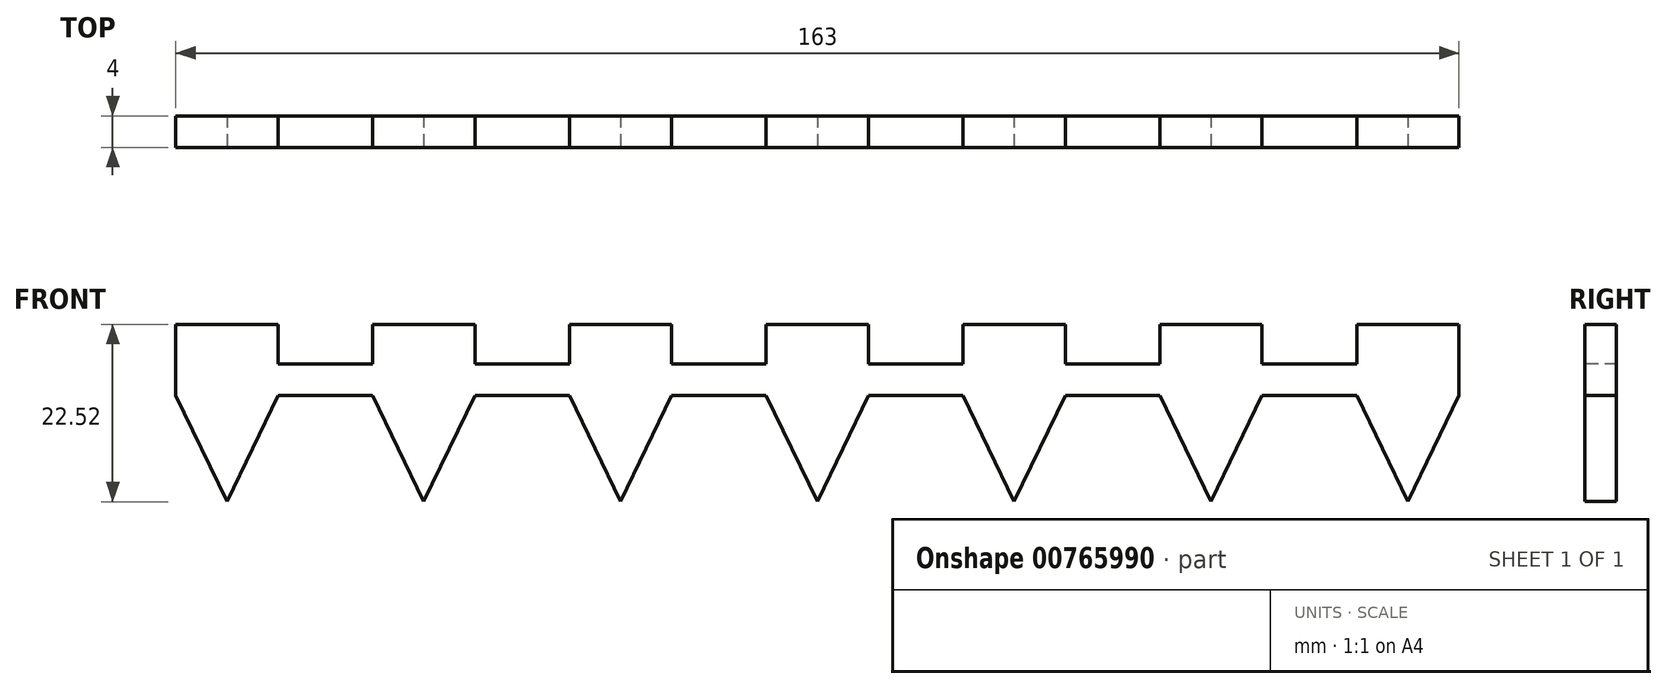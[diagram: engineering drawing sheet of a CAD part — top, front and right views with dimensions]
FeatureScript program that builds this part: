
annotation { "Feature Type Name" : "Feature", "Feature Type Description" : "" }
export const myFeature = defineFeature(function(context is Context, id is Id, definition is map)
    precondition{}
    {
        {
            var Q0;
            Q0=qCreatedBy(makeId("Top.planeOp"),FACE);
            var sketch = newSketch(context, id + "F0", { "sketchPlane" : qUnion([Q0])});
            skLineSegment(sketch, "E0.bottom", {"start": v(0, 0) * mm, "end": v(13, 0) * mm});
            skLineSegment(sketch, "E0.top", {"start": v(0, 4) * mm, "end": v(13, 4) * mm});
            skLineSegment(sketch, "E0.left", {"start": v(0, 0) * mm, "end": v(0, 4) * mm});
            skLineSegment(sketch, "E0.right", {"start": v(13, 0) * mm, "end": v(13, 4) * mm});
            skLineSegment(sketch, "E1.1.0.0", {"start": v(25, 4) * mm, "end": v(38, 4) * mm});
            skLineSegment(sketch, "E1.1.0.1", {"start": v(25, 0) * mm, "end": v(38, 0) * mm});
            skLineSegment(sketch, "E1.1.0.2", {"start": v(25, 0) * mm, "end": v(25, 4) * mm});
            skLineSegment(sketch, "E1.1.0.3", {"start": v(38, 0) * mm, "end": v(38, 4) * mm});
            skLineSegment(sketch, "E1.2.0.0", {"start": v(50, 4) * mm, "end": v(63, 4) * mm});
            skLineSegment(sketch, "E1.2.0.1", {"start": v(50, 0) * mm, "end": v(63, 0) * mm});
            skLineSegment(sketch, "E1.2.0.2", {"start": v(50, 0) * mm, "end": v(50, 4) * mm});
            skLineSegment(sketch, "E1.2.0.3", {"start": v(63, 0) * mm, "end": v(63, 4) * mm});
            skLineSegment(sketch, "E1.3.0.0", {"start": v(75, 4) * mm, "end": v(88, 4) * mm});
            skLineSegment(sketch, "E1.3.0.1", {"start": v(75, 0) * mm, "end": v(88, 0) * mm});
            skLineSegment(sketch, "E1.3.0.2", {"start": v(75, 0) * mm, "end": v(75, 4) * mm});
            skLineSegment(sketch, "E1.3.0.3", {"start": v(88, 0) * mm, "end": v(88, 4) * mm});
            skLineSegment(sketch, "E1.4.0.0", {"start": v(100, 4) * mm, "end": v(113, 4) * mm});
            skLineSegment(sketch, "E1.4.0.1", {"start": v(100, 0) * mm, "end": v(113, 0) * mm});
            skLineSegment(sketch, "E1.4.0.2", {"start": v(100, 0) * mm, "end": v(100, 4) * mm});
            skLineSegment(sketch, "E1.4.0.3", {"start": v(113, 0) * mm, "end": v(113, 4) * mm});
            skLineSegment(sketch, "E1.5.0.0", {"start": v(125, 4) * mm, "end": v(138, 4) * mm});
            skLineSegment(sketch, "E1.5.0.1", {"start": v(125, 0) * mm, "end": v(138, 0) * mm});
            skLineSegment(sketch, "E1.5.0.2", {"start": v(125, 0) * mm, "end": v(125, 4) * mm});
            skLineSegment(sketch, "E1.5.0.3", {"start": v(138, 0) * mm, "end": v(138, 4) * mm});
            skLineSegment(sketch, "E1.direction1", {"start": v(0, 0) * mm, "end": v(25, 0) * mm, "construction": true});
            skLineSegment(sketch, "E2.bottom", {"start": v(0, 4) * mm, "end": v(138, 4) * mm});
            skLineSegment(sketch, "E2.top", {"start": v(0, 0) * mm, "end": v(138, 0) * mm});
            skLineSegment(sketch, "E2.left", {"start": v(0, 4) * mm, "end": v(0, 0) * mm});
            skLineSegment(sketch, "E2.right", {"start": v(138, 4) * mm, "end": v(138, 0) * mm});
            skLineSegment(sketch, "E3.0.6.0", {"start": v(150, 4) * mm, "end": v(163, 4) * mm});
            skLineSegment(sketch, "E3.3.6.0", {"start": v(150, 0) * mm, "end": v(163, 0) * mm});
            skLineSegment(sketch, "E3.6.6.0", {"start": v(150, 0) * mm, "end": v(150, 4) * mm});
            skLineSegment(sketch, "E3.9.6.0", {"start": v(163, 0) * mm, "end": v(163, 4) * mm});
            skLineSegment(sketch, "E4", {"start": v(138, 4) * mm, "end": v(150, 4) * mm});
            skLineSegment(sketch, "E5", {"start": v(138, 0) * mm, "end": v(150, 0) * mm});
            skSolve(sketch);
        }
        {
            var Q0;
            Q0=qSketchRegion(id+"F0",true);
            extrude(context, id + "F1", {"entities" : qUnion([Q0]), "depth" : 4 * mm, "offsetDistance" : 25 * mm});
        }
        {
            var Q0;
            {var subQ0=sQuery(id+"F0.wireOp",EDGE,"E0.right");Q0=makeQuery(id+"F0.imprint","IMPRINT",FACE,{"disambiguationData":[TD([[makeQuery(id+"F0.imprint","IMPRINT",EDGE,{"derivedFrom":subQ0}),1.0]])]});}
            var Q1;
            {var subQ0=sQuery(id+"F0.wireOp",EDGE,"E1.1.0.2");Q1=makeQuery(id+"F0.imprint","IMPRINT",FACE,{"disambiguationData":[TD([[makeQuery(id+"F0.imprint","IMPRINT",EDGE,{"derivedFrom":subQ0}),-1.0]])]});}
            var Q2;
            {var subQ0=sQuery(id+"F0.wireOp",EDGE,"E1.2.0.2");Q2=makeQuery(id+"F0.imprint","IMPRINT",FACE,{"disambiguationData":[TD([[makeQuery(id+"F0.imprint","IMPRINT",EDGE,{"derivedFrom":subQ0}),-1.0]])]});}
            var Q3;
            {var subQ0=sQuery(id+"F0.wireOp",EDGE,"E1.3.0.2");Q3=makeQuery(id+"F0.imprint","IMPRINT",FACE,{"disambiguationData":[TD([[makeQuery(id+"F0.imprint","IMPRINT",EDGE,{"derivedFrom":subQ0}),-1.0]])]});}
            var Q4;
            {var subQ0=sQuery(id+"F0.wireOp",EDGE,"E1.4.0.2");Q4=makeQuery(id+"F0.imprint","IMPRINT",FACE,{"disambiguationData":[TD([[makeQuery(id+"F0.imprint","IMPRINT",EDGE,{"derivedFrom":subQ0}),-1.0]])]});}
            var Q5;
            {var subQ0=sQuery(id+"F0.wireOp",EDGE,"E1.5.0.2");Q5=makeQuery(id+"F0.imprint","IMPRINT",FACE,{"disambiguationData":[TD([[makeQuery(id+"F0.imprint","IMPRINT",EDGE,{"derivedFrom":subQ0}),-1.0]])]});}
            var Q6;
            Q6=makeQuery(id+"F0.imprint","IMPRINT",FACE,{"disambiguationData":[TD([[makeQuery(id+"F0.imprint","IMPRINT",EDGE,{"derivedFrom":sQuery(id+"F0.wireOp",EDGE,"E3.0.6.0")}),-1.0]])]});
            extrude(context, id + "F2", {"entities" : qUnion([Q0, Q1, Q2, Q3, Q4, Q5, Q6]), "operationType" : NewBodyOperationType.ADD, "depth" : 9 * mm, "offsetDistance" : 25 * mm});
        }
        {
            var Q0;
            {var subQ0=sQuery(id+"F0.wireOp",EDGE,"E2.top");Q0=makeQuery(id+"F2.boolean.opBoolean","MERGE",FACE,{"derivedFrom":[makeQuery(id+"F1.opExtrude","SWEPT_FACE",FACE,{"disambiguationData":[OSD([subQ0])]}),makeQuery(id+"F2.opExtrude","SWEPT_FACE",FACE,{"disambiguationData":[OSD([subQ0]),TDD([makeQuery(id+"F0.imprint","IMPRINT",EDGE,{"disambiguationData":[TD([[makeQuery(id+"F0.imprint","INTERSECT",VERTEX,{"derivedFrom":[sQuery(id+"F0.wireOp",EDGE,"E0.right"),subQ0]}),1.0]])],"derivedFrom":subQ0})])]}),makeQuery(id+"F2.opExtrude","SWEPT_FACE",FACE,{"disambiguationData":[OSD([subQ0]),TDD([makeQuery(id+"F0.imprint","IMPRINT",EDGE,{"disambiguationData":[TD([[makeQuery(id+"F0.imprint","INTERSECT",VERTEX,{"derivedFrom":[sQuery(id+"F0.wireOp",EDGE,"E1.1.0.2"),subQ0]}),-1.0]])],"derivedFrom":subQ0})])]}),makeQuery(id+"F2.opExtrude","SWEPT_FACE",FACE,{"disambiguationData":[OSD([subQ0]),TDD([makeQuery(id+"F0.imprint","IMPRINT",EDGE,{"disambiguationData":[TD([[makeQuery(id+"F0.imprint","INTERSECT",VERTEX,{"derivedFrom":[sQuery(id+"F0.wireOp",EDGE,"E1.2.0.2"),subQ0]}),-1.0]])],"derivedFrom":subQ0})])]}),makeQuery(id+"F2.opExtrude","SWEPT_FACE",FACE,{"disambiguationData":[OSD([subQ0]),TDD([makeQuery(id+"F0.imprint","IMPRINT",EDGE,{"disambiguationData":[TD([[makeQuery(id+"F0.imprint","INTERSECT",VERTEX,{"derivedFrom":[sQuery(id+"F0.wireOp",EDGE,"E1.3.0.2"),subQ0]}),-1.0]])],"derivedFrom":subQ0})])]}),makeQuery(id+"F2.opExtrude","SWEPT_FACE",FACE,{"disambiguationData":[OSD([subQ0]),TDD([makeQuery(id+"F0.imprint","IMPRINT",EDGE,{"disambiguationData":[TD([[makeQuery(id+"F0.imprint","INTERSECT",VERTEX,{"derivedFrom":[sQuery(id+"F0.wireOp",EDGE,"E1.4.0.2"),subQ0]}),-1.0]])],"derivedFrom":subQ0})])]}),makeQuery(id+"F2.opExtrude","SWEPT_FACE",FACE,{"disambiguationData":[OSD([subQ0]),TDD([makeQuery(id+"F0.imprint","IMPRINT",EDGE,{"disambiguationData":[TD([[makeQuery(id+"F0.imprint","INTERSECT",VERTEX,{"derivedFrom":[sQuery(id+"F0.wireOp",EDGE,"E1.5.0.2"),subQ0]}),-1.0]])],"derivedFrom":subQ0})])]})]});}
            var sketch = newSketch(context, id + "F3", { "sketchPlane" : qUnion([Q0])});
            skPoint(sketch, "E6.0", {"position": v(0, 0) * mm});
            skPoint(sketch, "E7.0", {"position": v(13, 0) * mm});
            skPoint(sketch, "E8.0", {"position": v(25, 0) * mm});
            skPoint(sketch, "E9.0", {"position": v(38, 0) * mm});
            skPoint(sketch, "E10.0", {"position": v(50, 0) * mm});
            skPoint(sketch, "E11.0", {"position": v(63, 0) * mm});
            skPoint(sketch, "E12.0", {"position": v(75, 0) * mm});
            skPoint(sketch, "E13.0", {"position": v(88, 0) * mm});
            skPoint(sketch, "E14.0", {"position": v(100, 0) * mm});
            skPoint(sketch, "E15.0", {"position": v(113, 0) * mm});
            skPoint(sketch, "E16.0", {"position": v(125, 0) * mm});
            skPoint(sketch, "E17.0", {"position": v(138, 0) * mm});
            skLineSegment(sketch, "E18", {"start": v(0, 0) * mm, "end": v(6.5, -13.52) * mm});
            skLineSegment(sketch, "E19", {"start": v(6.5, -13.52) * mm, "end": v(13, 0) * mm});
            skLineSegment(sketch, "E20", {"start": v(25, 0) * mm, "end": v(31.5, -13.52) * mm});
            skLineSegment(sketch, "E21", {"start": v(31.5, -13.52) * mm, "end": v(38, 0) * mm});
            skLineSegment(sketch, "E22", {"start": v(50, 0) * mm, "end": v(56.5, -13.52) * mm});
            skLineSegment(sketch, "E23", {"start": v(56.5, -13.52) * mm, "end": v(63, 0) * mm});
            skLineSegment(sketch, "E24", {"start": v(75, 0) * mm, "end": v(81.5, -13.52) * mm});
            skLineSegment(sketch, "E25", {"start": v(81.5, -13.52) * mm, "end": v(88, 0) * mm});
            skLineSegment(sketch, "E26", {"start": v(100, 0) * mm, "end": v(106.5, -13.52) * mm});
            skLineSegment(sketch, "E27", {"start": v(106.5, -13.52) * mm, "end": v(113, 0) * mm});
            skLineSegment(sketch, "E28", {"start": v(125, 0) * mm, "end": v(131.5, -13.52) * mm});
            skLineSegment(sketch, "E29", {"start": v(131.5, -13.52) * mm, "end": v(138, 0) * mm});
            skPoint(sketch, "E30.0", {"position": v(150, 0) * mm});
            skPoint(sketch, "E31.0", {"position": v(163, 0) * mm});
            skLineSegment(sketch, "E32", {"start": v(150, 0) * mm, "end": v(156.5, -13.52) * mm});
            skLineSegment(sketch, "E33", {"start": v(156.5, -13.52) * mm, "end": v(163, 0) * mm});
            skLineSegment(sketch, "E34", {"start": v(156.5, -13.52) * mm, "end": v(156.5, 0) * mm, "construction": true});
            skSolve(sketch);
        }
        {
            var Q0;
            {var subQ0=sQuery(id+"F3.wireOp",EDGE,"E18");Q0=makeQuery(id+"F3.imprint","IMPRINT",FACE,{"disambiguationData":[TD([[makeQuery(id+"F3.imprint","IMPRINT",EDGE,{"derivedFrom":subQ0}),1.0]])]});}
            var Q1;
            {var subQ0=sQuery(id+"F3.wireOp",EDGE,"E20");Q1=makeQuery(id+"F3.imprint","IMPRINT",FACE,{"disambiguationData":[TD([[makeQuery(id+"F3.imprint","IMPRINT",EDGE,{"derivedFrom":subQ0}),1.0]])]});}
            var Q2;
            {var subQ0=sQuery(id+"F3.wireOp",EDGE,"E22");Q2=makeQuery(id+"F3.imprint","IMPRINT",FACE,{"disambiguationData":[TD([[makeQuery(id+"F3.imprint","IMPRINT",EDGE,{"derivedFrom":subQ0}),1.0]])]});}
            var Q3;
            {var subQ0=sQuery(id+"F3.wireOp",EDGE,"E24");Q3=makeQuery(id+"F3.imprint","IMPRINT",FACE,{"disambiguationData":[TD([[makeQuery(id+"F3.imprint","IMPRINT",EDGE,{"derivedFrom":subQ0}),1.0]])]});}
            var Q4;
            {var subQ0=sQuery(id+"F3.wireOp",EDGE,"E26");Q4=makeQuery(id+"F3.imprint","IMPRINT",FACE,{"disambiguationData":[TD([[makeQuery(id+"F3.imprint","IMPRINT",EDGE,{"derivedFrom":subQ0}),1.0]])]});}
            var Q5;
            {var subQ0=sQuery(id+"F3.wireOp",EDGE,"E28");Q5=makeQuery(id+"F3.imprint","IMPRINT",FACE,{"disambiguationData":[TD([[makeQuery(id+"F3.imprint","IMPRINT",EDGE,{"derivedFrom":subQ0}),1.0]])]});}
            var Q6;
            {var subQ0=sQuery(id+"F3.wireOp",EDGE,"E32");Q6=makeQuery(id+"F3.imprint","IMPRINT",FACE,{"disambiguationData":[TD([[makeQuery(id+"F3.imprint","IMPRINT",EDGE,{"derivedFrom":subQ0}),1.0]])]});}
            extrude(context, id + "F4", {"entities" : qUnion([Q0, Q1, Q2, Q3, Q4, Q5, Q6]), "operationType" : NewBodyOperationType.ADD, "oppositeDirection" : true, "depth" : 4 * mm, "offsetDistance" : 25 * mm});
        }
    });
